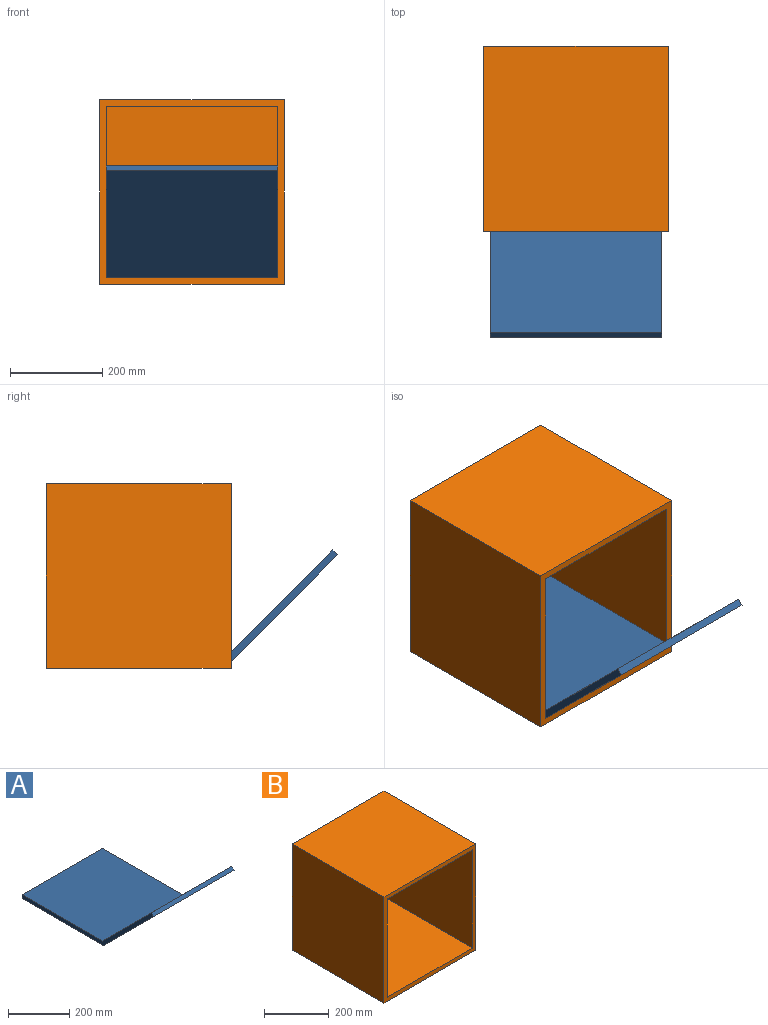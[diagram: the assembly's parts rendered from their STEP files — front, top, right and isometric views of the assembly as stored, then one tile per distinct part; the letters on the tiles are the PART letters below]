
ASSEMBLY  parts=2 mates=1
PART A: 8 faces, bbox 370x606.9x241.3 mm
  f0: plane 370x370mm, normal (0,0,1), area 136900mm2, adj f1,f5,f6,f7
  f1: plane 370x226.27mm, normal (0,0.71,0.71), area 118400mm2, adj f0,f2,f6,f7
  f2: plane 370x10.61mm, normal (0,-0.71,0.71), area 5550mm2, adj f1,f3,f6,f7
  f3: plane 370x230.67mm, normal (0,-0.71,-0.71), area 120698.9mm2, adj f2,f4,f6,f7
  f4: plane 376.21x370mm, normal (0,0,-1), area 139198.9mm2, adj f3,f5,f6,f7
  f5: plane 370x15mm, normal (0,1,0), area 5550mm2, adj f0,f4,f6,f7
  f6: plane 606.88x241.27mm, normal (1,0,0), area 10443.2mm2, adj f0,f1,f2,f3,f4,f5
  f7: plane 606.88x241.27mm, normal (-1,0,0), area 10443.2mm2, adj f0,f1,f2,f3,f4,f5
PART B: 11 faces, bbox 400x400x400 mm
  f0: plane 400x400mm, normal (0,-1,0), area 23100mm2, adj f2,f3,f4,f5,f7,f8,f9,f10
  f1: plane 400x400mm, normal (0,1,0), area 160000mm2, adj f2,f3,f4,f5
  f2: plane 400x400mm, normal (-1,0,0), area 160000mm2, adj f0,f1,f4,f5
  f3: plane 400x400mm, normal (1,0,0), area 160000mm2, adj f0,f1,f4,f5
  f4: plane 400x400mm, normal (0,0,1), area 160000mm2, adj f0,f1,f2,f3
  f5: plane 400x400mm, normal (0,0,-1), area 160000mm2, adj f0,f1,f2,f3
  f6: plane 370x370mm, normal (0,-1,0), area 136900mm2, adj f7,f8,f9,f10
  f7: plane 385x370mm, normal (1,0,0), area 142450mm2, adj f0,f6,f9,f10
  f8: plane 385x370mm, normal (-1,0,0), area 142450mm2, adj f0,f6,f9,f10
  f9: plane 385x370mm, normal (0,0,-1), area 142450mm2, adj f0,f6,f7,f8
  f10: plane 385x370mm, normal (0,0,1), area 142450mm2, adj f0,f6,f7,f8
PLACE A rot(axis=(-1,0,0),0deg) t=(-627.5,-217.21,65.17)mm
PLACE B t=(-442.5,-23.42,35.17)mm fixed
MATE revolute B.f7 <-> A.f7  axis (1,0,0) through (-627.5,-223.42,50.17)mm
